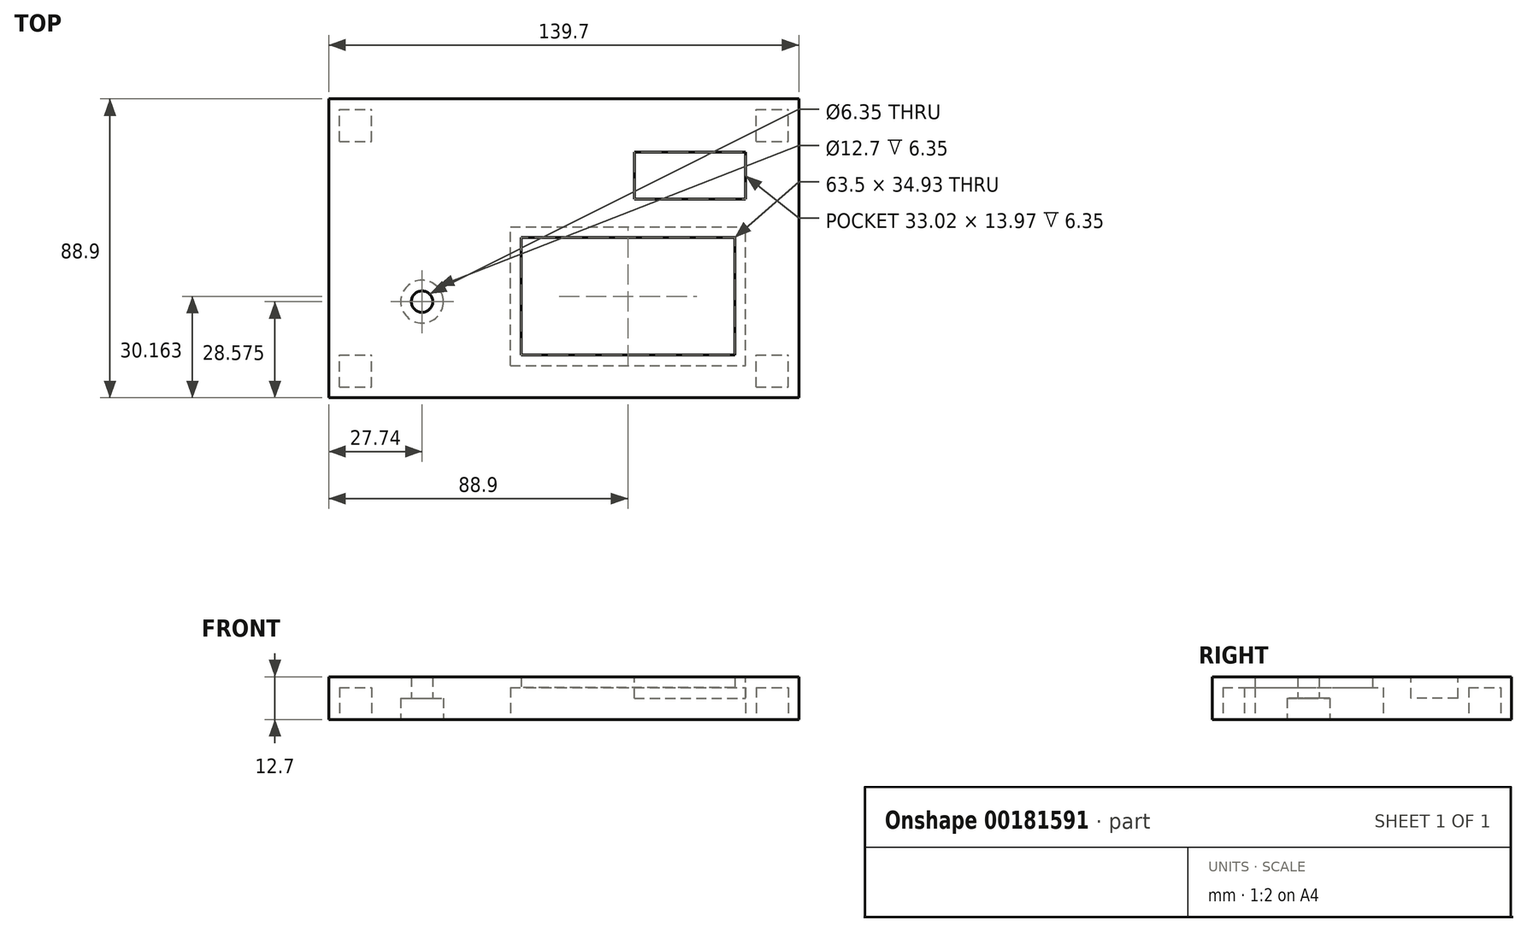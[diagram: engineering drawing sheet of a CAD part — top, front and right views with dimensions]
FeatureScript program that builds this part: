
annotation { "Feature Type Name" : "Feature", "Feature Type Description" : "" }
export const myFeature = defineFeature(function(context is Context, id is Id, definition is map)
    precondition{}
    {
        {
            var Q0;
            Q0=qCreatedBy(makeId("Top.planeOp"),FACE);
            var sketch = newSketch(context, id + "F0", { "sketchPlane" : qUnion([Q0])});
            skLineSegment(sketch, "E0.bottom", {"start": v(0, 0) * mm, "end": v(-139.7, 0) * mm});
            skLineSegment(sketch, "E0.top", {"start": v(0, -88.9) * mm, "end": v(-139.7, -88.9) * mm});
            skLineSegment(sketch, "E0.left", {"start": v(0, 0) * mm, "end": v(0, -88.9) * mm});
            skLineSegment(sketch, "E0.right", {"start": v(-139.7, 0) * mm, "end": v(-139.7, -88.9) * mm});
            skLineSegment(sketch, "E1.bottom", {"start": v(-82.55, -41.28) * mm, "end": v(-19.05, -41.28) * mm});
            skLineSegment(sketch, "E1.top", {"start": v(-82.55, -76.2) * mm, "end": v(-19.05, -76.2) * mm});
            skLineSegment(sketch, "E1.left", {"start": v(-82.55, -41.28) * mm, "end": v(-82.55, -76.2) * mm});
            skLineSegment(sketch, "E1.right", {"start": v(-19.05, -41.28) * mm, "end": v(-19.05, -76.2) * mm});
            skSolve(sketch);
        }
        {
            var Q0;
            Q0=makeQuery(id+"F0.imprint","IMPRINT",FACE,{"disambiguationData":[TD([[makeQuery(id+"F0.imprint","IMPRINT",EDGE,{"derivedFrom":sQuery(id+"F0.wireOp",EDGE,"E0.bottom")}),1.0]])]});
            extrude(context, id + "F1", {"entities" : qUnion([Q0]), "depth" : 12.7 * mm});
        }
        {
            var Q0;
            Q0=makeQuery(id+"F1.opExtrude","CAP_FACE",FACE,{"disambiguationData":[OSD([sQuery(id+"F0.wireOp",EDGE,"E0.bottom"),sQuery(id+"F0.wireOp",EDGE,"E0.top"),sQuery(id+"F0.wireOp",EDGE,"E0.left"),sQuery(id+"F0.wireOp",EDGE,"E0.right"),sQuery(id+"F0.wireOp",EDGE,"E1.bottom"),sQuery(id+"F0.wireOp",EDGE,"E1.top"),sQuery(id+"F0.wireOp",EDGE,"E1.left"),sQuery(id+"F0.wireOp",EDGE,"E1.right")])],"isStart":true});
            var sketch = newSketch(context, id + "F2", { "sketchPlane" : qUnion([Q0])});
            skLineSegment(sketch, "E2.bottom", {"start": v(-136.53, 12.7) * mm, "end": v(-127, 12.7) * mm});
            skLineSegment(sketch, "E2.top", {"start": v(-136.53, 3.17) * mm, "end": v(-127, 3.18) * mm});
            skLineSegment(sketch, "E2.left", {"start": v(-136.53, 12.7) * mm, "end": v(-136.53, 3.17) * mm});
            skLineSegment(sketch, "E2.right", {"start": v(-127, 12.7) * mm, "end": v(-127, 3.18) * mm});
            skLineSegment(sketch, "E3.0.1.0", {"start": v(-136.53, 85.73) * mm, "end": v(-127, 85.73) * mm});
            skLineSegment(sketch, "E3.0.1.1", {"start": v(-127, 85.73) * mm, "end": v(-127, 76.2) * mm});
            skLineSegment(sketch, "E3.0.1.2", {"start": v(-136.53, 76.2) * mm, "end": v(-127, 76.2) * mm});
            skLineSegment(sketch, "E3.0.1.3", {"start": v(-136.53, 85.73) * mm, "end": v(-136.53, 76.2) * mm});
            skLineSegment(sketch, "E3.1.0.0", {"start": v(-12.7, 12.7) * mm, "end": v(-3.17, 12.7) * mm});
            skLineSegment(sketch, "E3.1.0.1", {"start": v(-3.17, 12.7) * mm, "end": v(-3.17, 3.18) * mm});
            skLineSegment(sketch, "E3.1.0.2", {"start": v(-12.7, 3.17) * mm, "end": v(-3.17, 3.18) * mm});
            skLineSegment(sketch, "E3.1.0.3", {"start": v(-12.7, 12.7) * mm, "end": v(-12.7, 3.17) * mm});
            skLineSegment(sketch, "E3.1.1.0", {"start": v(-12.7, 85.73) * mm, "end": v(-3.17, 85.73) * mm});
            skLineSegment(sketch, "E3.1.1.1", {"start": v(-3.17, 85.73) * mm, "end": v(-3.17, 76.2) * mm});
            skLineSegment(sketch, "E3.1.1.2", {"start": v(-12.7, 76.2) * mm, "end": v(-3.17, 76.2) * mm});
            skLineSegment(sketch, "E3.1.1.3", {"start": v(-12.7, 85.73) * mm, "end": v(-12.7, 76.2) * mm});
            skLineSegment(sketch, "E3.direction1", {"start": v(-136.53, 12.7) * mm, "end": v(-12.7, 12.7) * mm, "construction": true});
            skLineSegment(sketch, "E3.direction2", {"start": v(-136.53, 12.7) * mm, "end": v(-136.53, 85.73) * mm, "construction": true});
            skLineSegment(sketch, "E4.bottom", {"start": v(-85.72, 79.38) * mm, "end": v(-15.87, 79.38) * mm});
            skLineSegment(sketch, "E4.top", {"start": v(-85.72, 38.1) * mm, "end": v(-15.87, 38.1) * mm});
            skLineSegment(sketch, "E4.left", {"start": v(-85.72, 79.38) * mm, "end": v(-85.72, 38.1) * mm});
            skLineSegment(sketch, "E4.right", {"start": v(-15.87, 79.38) * mm, "end": v(-15.87, 38.1) * mm});
            skSolve(sketch);
        }
        {
            var Q0;
            Q0 = qSketchRegion(id + "F2", true);
            extrude(context, id + "F3", {"entities" : qUnion([Q0]), "operationType" : NewBodyOperationType.REMOVE, "oppositeDirection" : true, "depth" : 9.52 * mm});
        }
        {
            var Q0;
            Q0=makeQuery(id+"F1.opExtrude","CAP_FACE",FACE,{"disambiguationData":[OSD([sQuery(id+"F0.wireOp",EDGE,"E0.bottom"),sQuery(id+"F0.wireOp",EDGE,"E0.top"),sQuery(id+"F0.wireOp",EDGE,"E0.left"),sQuery(id+"F0.wireOp",EDGE,"E0.right"),sQuery(id+"F0.wireOp",EDGE,"E1.bottom"),sQuery(id+"F0.wireOp",EDGE,"E1.top"),sQuery(id+"F0.wireOp",EDGE,"E1.left"),sQuery(id+"F0.wireOp",EDGE,"E1.right")])],"isStart":false});
            var sketch = newSketch(context, id + "F4", { "sketchPlane" : qUnion([Q0])});
            skLineSegment(sketch, "E5.bottom", {"start": v(-48.9, -15.88) * mm, "end": v(-15.88, -15.87) * mm});
            skLineSegment(sketch, "E5.top", {"start": v(-48.9, -29.84) * mm, "end": v(-15.88, -29.84) * mm});
            skLineSegment(sketch, "E5.left", {"start": v(-48.9, -15.88) * mm, "end": v(-48.9, -29.85) * mm});
            skLineSegment(sketch, "E5.right", {"start": v(-15.88, -15.87) * mm, "end": v(-15.88, -29.84) * mm});
            skSolve(sketch);
        }
        {
            var Q0;
            Q0 = qSketchRegion(id + "F4", true);
            extrude(context, id + "F5", {"entities" : qUnion([Q0]), "operationType" : NewBodyOperationType.REMOVE, "oppositeDirection" : true, "depth" : 6.35 * mm});
        }
        {
            var Q0;
            Q0=makeQuery(id+"F1.opExtrude","CAP_FACE",FACE,{"disambiguationData":[OSD([sQuery(id+"F0.wireOp",EDGE,"E0.bottom"),sQuery(id+"F0.wireOp",EDGE,"E0.top"),sQuery(id+"F0.wireOp",EDGE,"E0.left"),sQuery(id+"F0.wireOp",EDGE,"E0.right"),sQuery(id+"F0.wireOp",EDGE,"E1.bottom"),sQuery(id+"F0.wireOp",EDGE,"E1.top"),sQuery(id+"F0.wireOp",EDGE,"E1.left"),sQuery(id+"F0.wireOp",EDGE,"E1.right")])],"isStart":true});
            var sketch = newSketch(context, id + "F6", { "sketchPlane" : qUnion([Q0])});
            skPoint(sketch, "E6", {"position": v(-111.96, 60.33) * mm});
            skSolve(sketch);
        }
        {
            var Q0;
            Q0=sQuery(id+"F6.wireOp",VERTEX,"E6");
            var Q1;
            Q1=makeQuery(id+"F1.opExtrude","SWEPT_BODY",BODY,{"disambiguationData":[OSD([sQuery(id+"F0.wireOp",EDGE,"E0.bottom"),sQuery(id+"F0.wireOp",EDGE,"E0.top"),sQuery(id+"F0.wireOp",EDGE,"E0.left"),sQuery(id+"F0.wireOp",EDGE,"E0.right"),sQuery(id+"F0.wireOp",EDGE,"E1.bottom"),sQuery(id+"F0.wireOp",EDGE,"E1.top"),sQuery(id+"F0.wireOp",EDGE,"E1.left"),sQuery(id+"F0.wireOp",EDGE,"E1.right")])]});
            hole(context, id + "F7", {"style" : HoleStyle.C_BORE, "endStyle" : HoleEndStyle.THROUGH, "holeDiameter" : 6.35 * mm, "cBoreDiameter" : 12.7 * mm, "cBoreDepth" : 6.35 * mm, "locations" : qUnion([Q0]), "scope" : qUnion([Q1]), "isTappedThrough" : true});
        }
    });
